# Revit family: Sanitary_Shower-screens_Duscholux_Plus Evolution_3-Slider-doors-shower
name_source: partatom
category: Plumbing Fixtures
revit_build: Autodesk Revit 2016 (Build: 20150220_1215(x64)
units: mm (PartAtom-declared; Revit-internal decimal feet)

## family parameters
Always vertical = Yes
Cut with Voids When Loaded = No
OmniClass Number = 23.45.00.00
OmniClass Title = Sanitary, Laundry, and Cleaning Equipment
Part Type = Normal
Room Calculation Point = No
Round Connector Dimension = Use Diameter
Shared = No
Work Plane-Based = No

## types (3) — shared parameters
Anti-Lime Treatment = FeelNet 3D Included
Assembly Code = C1030200
Brand = Duscholux
Certified Quality UNE EN 14428 = http://www.duscholux.es
Combinations = Lateral 90°
Components = Eropean components
Configuration enclosure = http://configuratumampara.duscholux.es
Description = Front 1 fixed + 2 sliding doors shower
Design country = Spain / Germany
Edition number = 1
Environmental Management ISO 14001 = ECOEMBES Certificate
Fact Sheet = http://blob.duscholux.es
Glass Material = Glass_Material-Duscholux
Glass in Building UNE EN 12150 = CE Conformity marking
Height = 1900 mm  [stored 6.2336 ft]
IFC Classification = Furnishing Element
Image = https://www.duscholux.es
Maintenance and Cleaning = http://www.duscholux.es
Manufacturer = Duscholux Ibérica, S.A.
Manufacturer country = Spain
Manufacturer name = Duscholux Ibérica, S.A.
Max Height = 1900 mm  [stored 6.2336 ft]
Min Max Width = 1500 mm  [stored 4.92126 ft]
NBS Reference Code = 45-35-70
NBS Reference Description = Shower Enclosures
Net Weight (Kg) = 60
Opening System = Sliding
Opening System Image = http://blob.duscholux.es
Optional = Towel rail / Shelf
Product family = Plus Evolution
Product group = Front for shower
Products = http://www.duscholux.es
Ref. = 7BI / 7BD
Series = Plus Evolution
Sliding Door Width = 481 mm
Technical Inspection Certificate (Applus) = http://www.duscholux.es
Thickness Safety Glass Fixed Panel = 5 mm  [stored 0.0164042 ft]
Thickness Safety Glass Sliding = 5 mm  [stored 0.0164042 ft]
UNSPSC Code = 30181507
URL = http://www.duscholux.es
Uniclass 2015 Code = PR-40-20-06-79
Uniclass 2015 Description = Shower Enclosures
Width = 1500 mm  [stored 4.92126 ft]
zero-valued in all types: Opening Door 1, Opening Door 2, Opening Percentage

## per-type parameters (varying)
| type | Accesories Material | Handle Material |
| Platinum Aluminium Finish | Plastic, Gray | Silver Matt Aluminium Finish |
| White Aluminium Finish | White Finish | White Finish |
| Silver Matt Aluminium Finish | Plastic, Gray | Silver Matt Aluminium Finish |

note: column(s) folded — value = type name in every type: Frame Material

note: [stored X ft] marks values corroborated as IEEE doubles in the binary element streams (Revit-internal decimal feet)
